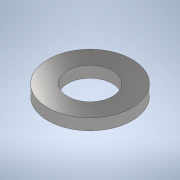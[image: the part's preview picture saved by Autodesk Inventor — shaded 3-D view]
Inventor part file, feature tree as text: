
AUTODESK INVENTOR PART (.ipt)
format: ipt  version: 2020.2 (Build 242310000, 310)  size: 102,912 bytes
history: native  units: mm
features: extrude x1, sketch x1
ambient origin geometry x8: Origin, YZ Plane, XZ Plane, XY Plane, X Axis, Y Axis, Z Axis, Center Point
bodies: Solido1 (feature_tree)
feature tree (2):
  extrude  "Estrusione1"  Depth=6.4mm
  sketch  "Schizzo1"
